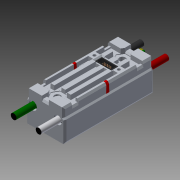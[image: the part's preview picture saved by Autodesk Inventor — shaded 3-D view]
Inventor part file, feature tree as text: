
AUTODESK INVENTOR PART (.ipt)
format: ipt  version: 2016 SP1 (Build 200210100, 210)  size: 3,524,608 bytes
history: native  units: in
note: dims shown in document units (in); Inventor stores cm internally (conversion verified against a paired STEP export)
features: plane x2, split x2, boolean_combine x1, imported_body x1
ambient origin geometry x8: Origin, YZ Plane, XZ Plane, XY Plane, X Axis, Y Axis, Z Axis, Center Point
bodies: Body1 (feature_tree)
feature tree (6):
  boolean_combine  "Combine11"
  plane  "Work Plane1"
  split  "Split1"
  plane  "Work Plane2"
  split  "Split2"
  imported_body  "Base1"
